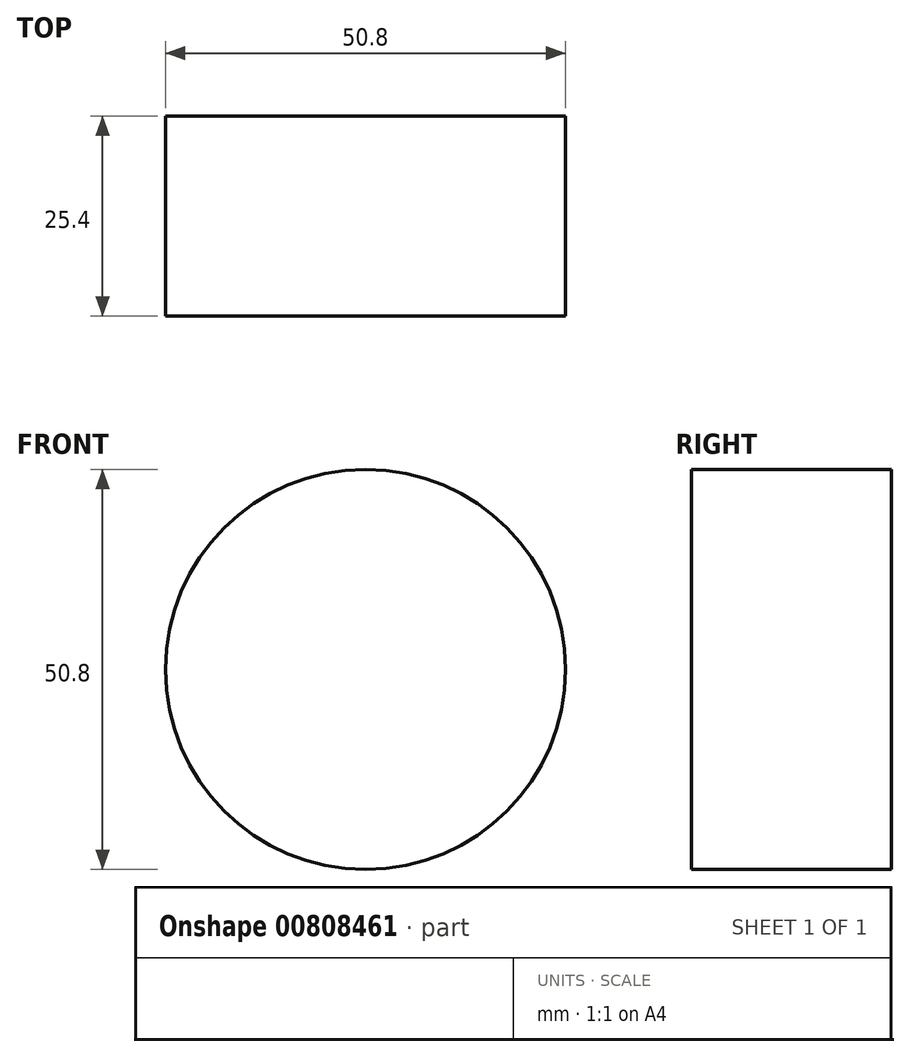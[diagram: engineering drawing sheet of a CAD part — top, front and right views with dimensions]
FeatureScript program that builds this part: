
annotation { "Feature Type Name" : "Feature", "Feature Type Description" : "" }
export const myFeature = defineFeature(function(context is Context, id is Id, definition is map)
    precondition{}
    {
        {
            var Q0;
            Q0=qCreatedBy(makeId("Front.planeOp"),FACE);
            var sketch = newSketch(context, id + "F0", { "sketchPlane" : qUnion([Q0])});
            skLineSegment(sketch, "E0", {"start": v(-29.19, 20.72) * mm, "end": v(-3.8, 20.72) * mm});
            skLineSegment(sketch, "E1", {"start": v(-41.89, 49.03) * mm, "end": v(-41.89, 33.42) * mm});
            skCircle(sketch, "E2", {"center": v(25.4, 45.45) * mm, "radius": 25.4 * mm});
            skArc(sketch, "E3.filletArc", {"start": v(-41.89, 33.42) * mm, "mid": v(-38.17, 24.44) * mm, "end": v(-29.19, 20.72) * mm});
            skLineSegment(sketch, "E4", {"start": v(0, 45.45) * mm, "end": v(0, 0) * mm});
            skSolve(sketch);
        }
        {
            var Q0;
            Q0=makeQuery(id+"F0.imprint","IMPRINT",FACE,{"disambiguationData":[TD([[makeQuery(id+"F0.imprint","IMPRINT",EDGE,{"derivedFrom":sQuery(id+"F0.wireOp",EDGE,"E2")}),1.0]])]});
            extrude(context, id + "F1", {"entities" : qUnion([Q0]), "depth" : 25.4 * mm, "offsetDistance" : 25.4 * mm});
        }
        {
            var Q0;
            Q0 = qSketchRegion(id + "F0", true);
            extrude(context, id + "F2", {"entities" : qUnion([Q0]), "operationType" : NewBodyOperationType.ADD, "depth" : 25.4 * mm, "offsetDistance" : 25.4 * mm});
        }
    });
